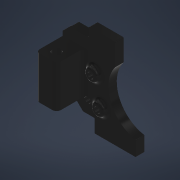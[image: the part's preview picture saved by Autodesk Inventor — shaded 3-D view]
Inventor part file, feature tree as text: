
AUTODESK INVENTOR PART (.ipt)
format: ipt  version: 2021 (Build 250183000, 183)  size: 400,384 bytes
history: native  units: mm
features: other x7, fillet x6, extrude x4, reference x4, plane x2, hole x1, projected_geometry x1
ambient origin geometry x8: Origin, YZ Plane, XZ Plane, XY Plane, X Axis, Y Axis, Z Axis, Center Point
bodies: Solid1 (feature_tree)
feature tree (25):
  plane  "Work Plane1"
  extrude  "plate"  Depth=2.8mm
  other  "plate_above"
  other  "arm_reference"
  plane  "Work Plane3"
  extrude  "arm_holder"  Depth=2.8mm
  fillet  "arm_holder_to_plate"  Radius=2.8mm
  extrude  "arm_hole"  Depth=4.96662mm
  fillet  "arm_holder_top"  Radius=2.48331mm
  fillet  "arm_holder_below_support1"  Radius=3.4mm
  fillet  "arm_holder_below_support2"  Radius=3.4mm
  hole  "hole_ext_sketch"  [1 undecoded]
  extrude  "hole_ext_tall"  Depth=3.65mm
  fillet  "hole_ext_top"  Radius=4.0mm
  fillet  "hole_ext_bottom"  Radius=0.3mm
  other  "plate_sketch"
  projected_geometry  "Projected Loop1"
  other  "arm_hole_sketch"
  reference  "Reference3"
  reference  "Reference4"
  reference  "Reference5"
  reference  "Reference6"
  other  "<userpath>\Documents\Dev\tco-cad\camera_mount\assembly_linear_stepper.iam"
  other  "assembly_linear_stepper.iam"
  other  "linear_stepper_carriage:1"
note: 1 required parameter value undecoded (feature->parameter linkage not recoverable at this tier; creation-order binding heuristic only, values carry confidence <= 0.55)
